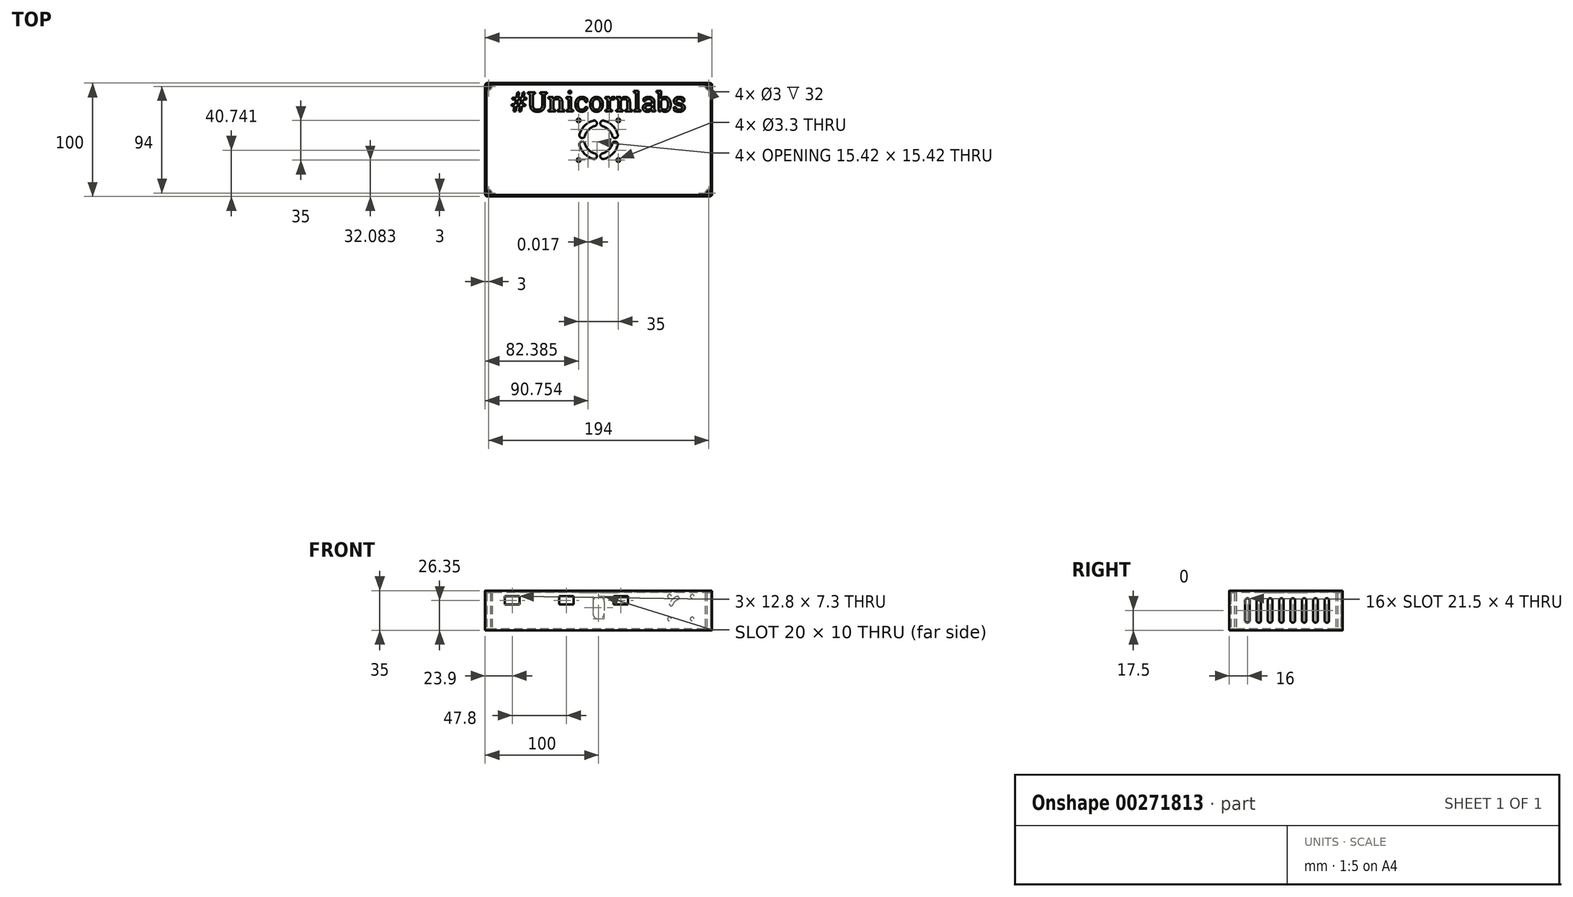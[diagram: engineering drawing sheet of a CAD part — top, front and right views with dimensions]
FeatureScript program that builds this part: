
annotation { "Feature Type Name" : "Feature", "Feature Type Description" : "" }
export const myFeature = defineFeature(function(context is Context, id is Id, definition is map)
    precondition{}
    {
        {
            assignVariable(context, id + "F0", {"name" : "CaseHeight", "anyValue" : 35});
        }
        {
            assignVariable(context, id + "F1", {"name" : "CaseWallThickness", "anyValue" : 1.2});
        }
        {
            assignVariable(context, id + "F2", {"name" : "MetricScrew", "anyValue" : 3});
        }
        {
            var Q0;
            Q0=qCreatedBy(makeId("Top.planeOp"),FACE);
            var sketch = newSketch(context, id + "F3", { "sketchPlane" : qUnion([Q0])});
            skLineSegment(sketch, "E0.bottom", {"start": v(100, 50) * mm, "end": v(-100, 50) * mm});
            skLineSegment(sketch, "E0.top", {"start": v(100, -50) * mm, "end": v(-100, -50) * mm});
            skLineSegment(sketch, "E0.left", {"start": v(100, 50) * mm, "end": v(100, -50) * mm});
            skLineSegment(sketch, "E0.right", {"start": v(-100, 50) * mm, "end": v(-100, -50) * mm});
            skPoint(sketch, "E0.middle", {"position": v(0, 0) * mm});
            skSolve(sketch);
        }
        {
            var Q0;
            Q0=makeQuery(id+"F3.imprint","IMPRINT",FACE,{"disambiguationData":[TD([[makeQuery(id+"F3.imprint","IMPRINT",EDGE,{"derivedFrom":sQuery(id+"F3.wireOp",EDGE,"E0.bottom")}),1.0]])]});
            extrude(context, id + "F4", {"entities" : qUnion([Q0]), "depth" : (getVariable(context, 'CaseHeight')) * mm});
        }
        {
            var Q0;
            Q0=makeQuery(id+"F4.opExtrude","CAP_FACE",FACE,{"disambiguationData":[OSD([sQuery(id+"F3.wireOp",EDGE,"E0.bottom"),sQuery(id+"F3.wireOp",EDGE,"E0.top"),sQuery(id+"F3.wireOp",EDGE,"E0.left"),sQuery(id+"F3.wireOp",EDGE,"E0.right")])],"isStart":false});
            shell(context, id + "F5", {"entities" : qUnion([Q0]), "thickness" : (getVariable(context, 'CaseWallThickness')) * mm});
        }
        {
            var Q0;
            Q0=makeQuery(id+"F5.opShell","OFFSET_FACE",FACE,{"disambiguationData":[OSD([sQuery(id+"F3.wireOp",EDGE,"E0.bottom"),sQuery(id+"F3.wireOp",EDGE,"E0.top"),sQuery(id+"F3.wireOp",EDGE,"E0.left"),sQuery(id+"F3.wireOp",EDGE,"E0.right")])]});
            var sketch = newSketch(context, id + "F6", { "sketchPlane" : qUnion([Q0])});
            skCircle(sketch, "E1", {"center": v(-97, 47) * mm, "radius": 1.5 * mm});
            skCircle(sketch, "E2", {"center": v(97, 47) * mm, "radius": 1.5 * mm});
            skCircle(sketch, "E3", {"center": v(97, -47) * mm, "radius": 1.5 * mm});
            skCircle(sketch, "E4", {"center": v(-97, -47) * mm, "radius": 1.5 * mm});
            skArc(sketch, "E5", {"start": v(-98.8, 44) * mm, "mid": v(-94.88, 44.88) * mm, "end": v(-94, 48.8) * mm});
            skArc(sketch, "E6.MirrorCS", {"start": v(98.8, 44) * mm, "mid": v(94.88, 44.88) * mm, "end": v(94, 48.8) * mm});
            skArc(sketch, "E7.MirrorCS", {"start": v(-98.8, -44) * mm, "mid": v(-94.88, -44.88) * mm, "end": v(-94, -48.8) * mm});
            skArc(sketch, "E8.MirrorCS", {"start": v(98.8, -44) * mm, "mid": v(94.88, -44.88) * mm, "end": v(94, -48.8) * mm});
            skSolve(sketch);
        }
        {
            var Q0;
            Q0=makeQuery(id+"F6.imprint","IMPRINT",FACE,{"disambiguationData":[TD([[makeQuery(id+"F6.imprint","IMPRINT",EDGE,{"derivedFrom":sQuery(id+"F6.wireOp",EDGE,"E1")}),-1.0]])]});
            var Q1;
            Q1=makeQuery(id+"F6.imprint","IMPRINT",FACE,{"disambiguationData":[TD([[makeQuery(id+"F6.imprint","IMPRINT",EDGE,{"derivedFrom":sQuery(id+"F6.wireOp",EDGE,"E2")}),-1.0]])]});
            var Q2;
            Q2=makeQuery(id+"F6.imprint","IMPRINT",FACE,{"disambiguationData":[TD([[makeQuery(id+"F6.imprint","IMPRINT",EDGE,{"derivedFrom":sQuery(id+"F6.wireOp",EDGE,"E3")}),-1.0]])]});
            var Q3;
            Q3=makeQuery(id+"F6.imprint","IMPRINT",FACE,{"disambiguationData":[TD([[makeQuery(id+"F6.imprint","IMPRINT",EDGE,{"derivedFrom":sQuery(id+"F6.wireOp",EDGE,"E4")}),-1.0]])]});
            extrude(context, id + "F7", {"entities" : qUnion([Q0, Q1, Q2, Q3]), "operationType" : NewBodyOperationType.ADD, "depth" : (getVariable(context, 'CaseHeight') - getVariable(context, 'MetricScrew')) * mm});
        }
        {
            var Q0;
            Q0=makeQuery(id+"F7.opExtrude","CAP_FACE",FACE,{"disambiguationData":[OSD([sQuery(id+"F3.wireOp",EDGE,"E0.bottom"),sQuery(id+"F3.wireOp",EDGE,"E0.right"),sQuery(id+"F6.wireOp",EDGE,"E1"),sQuery(id+"F6.wireOp",EDGE,"E5")])],"isStart":false});
            var sketch = newSketch(context, id + "F8", { "sketchPlane" : qUnion([Q0])});
            skPoint(sketch, "E9.0", {"position": v(98.8, -48.8) * mm});
            skPoint(sketch, "E10.0", {"position": v(-98.8, 48.8) * mm});
            skLineSegment(sketch, "E11.bottom", {"start": v(-98.8, 48.8) * mm, "end": v(98.8, 48.8) * mm});
            skLineSegment(sketch, "E11.top", {"start": v(-98.8, -48.8) * mm, "end": v(98.8, -48.8) * mm});
            skLineSegment(sketch, "E11.left", {"start": v(-98.8, 48.8) * mm, "end": v(-98.8, -48.8) * mm});
            skLineSegment(sketch, "E11.right", {"start": v(98.8, 48.8) * mm, "end": v(98.8, -48.8) * mm});
            skCircle(sketch, "E12.0", {"center": v(-97, 47) * mm, "radius": 1.5 * mm});
            skCircle(sketch, "E13.0", {"center": v(97, 47) * mm, "radius": 1.5 * mm});
            skCircle(sketch, "E14.0", {"center": v(97, -47) * mm, "radius": 1.5 * mm});
            skCircle(sketch, "E15.0", {"center": v(-97, -47) * mm, "radius": 1.5 * mm});
            skSolve(sketch);
        }
        {
            var Q0;
            Q0=makeQuery(id+"F8.imprint","IMPRINT",FACE,{"disambiguationData":[TD([[makeQuery(id+"F8.imprint","IMPRINT",EDGE,{"derivedFrom":sQuery(id+"F8.wireOp",EDGE,"E12.0")}),-1.0]])]});
            var Q1;
            {var subQ3=sQuery(id+"F8.wireOp",EDGE,"E11.top");Q1=makeQuery(id+"F8.imprint","IMPRINT",FACE,{"disambiguationData":[TD([[makeQuery(id+"F8.imprint","IMPRINT",EDGE,{"derivedFrom":subQ3}),1.0]])]});}
            extrude(context, id + "F9", {"entities" : qUnion([Q0, Q1]), "depth" : (getVariable(context, 'MetricScrew') / 2) * mm});
        }
        {
            var Q0;
            Q0=makeQuery(id+"F4.opExtrude","SWEPT_FACE",FACE,{"disambiguationData":[OSD([sQuery(id+"F3.wireOp",EDGE,"E0.top")])]});
            var sketch = newSketch(context, id + "F10", { "sketchPlane" : qUnion([Q0])});
            skLineSegment(sketch, "E16.bottom", {"start": v(-69.7, 30) * mm, "end": v(-82.5, 30) * mm});
            skLineSegment(sketch, "E16.top", {"start": v(-69.7, 22.7) * mm, "end": v(-82.5, 22.7) * mm});
            skLineSegment(sketch, "E16.left", {"start": v(-69.7, 30) * mm, "end": v(-69.7, 22.7) * mm});
            skLineSegment(sketch, "E16.right", {"start": v(-82.5, 30) * mm, "end": v(-82.5, 22.7) * mm});
            skPoint(sketch, "E16.middle", {"position": v(-76.1, 26.35) * mm});
            skLineSegment(sketch, "E17.1.0.0", {"start": v(-21.9, 30) * mm, "end": v(-21.9, 22.7) * mm});
            skLineSegment(sketch, "E17.1.0.1", {"start": v(-21.9, 30) * mm, "end": v(-34.7, 30) * mm});
            skLineSegment(sketch, "E17.1.0.2", {"start": v(-34.7, 30) * mm, "end": v(-34.7, 22.7) * mm});
            skLineSegment(sketch, "E17.1.0.3", {"start": v(-21.9, 22.7) * mm, "end": v(-34.7, 22.7) * mm});
            skLineSegment(sketch, "E17.2.0.0", {"start": v(25.9, 30) * mm, "end": v(25.9, 22.7) * mm});
            skLineSegment(sketch, "E17.2.0.1", {"start": v(25.9, 30) * mm, "end": v(13.1, 30) * mm});
            skLineSegment(sketch, "E17.2.0.2", {"start": v(13.1, 30) * mm, "end": v(13.1, 22.7) * mm});
            skLineSegment(sketch, "E17.2.0.3", {"start": v(25.9, 22.7) * mm, "end": v(13.1, 22.7) * mm});
            skLineSegment(sketch, "E17.direction1", {"start": v(-69.7, 22.7) * mm, "end": v(-21.9, 22.7) * mm, "construction": true});
            skSolve(sketch);
        }
        {
            var Q0;
            Q0=qSketchRegion(id+"F10",true);
            extrude(context, id + "F11", {"entities" : qUnion([Q0]), "operationType" : NewBodyOperationType.REMOVE, "oppositeDirection" : true, "depth" : (getVariable(context, 'CaseWallThickness')) * mm});
        }
        {
            var Q0;
            {var subQ0=sQuery(id+"F3.wireOp",EDGE,"E0.right");var subQ1=sQuery(id+"F3.wireOp",EDGE,"E0.left");var subQ2=sQuery(id+"F3.wireOp",EDGE,"E0.top");var subQ3=sQuery(id+"F3.wireOp",EDGE,"E0.bottom");Q0=makeQuery(id+"F7.boolean.opBoolean","SPLIT",FACE,{"disambiguationData":[TD([makeQuery(id+"F5.opShell","OFFSET_FACE",FACE,{"disambiguationData":[OSD([subQ3])]})])],"derivedFrom":makeQuery(id+"F5.opShell","OFFSET_FACE",FACE,{"disambiguationData":[OSD([subQ3,subQ2,subQ1,subQ0])]})});}
            var sketch = newSketch(context, id + "F12", { "sketchPlane" : qUnion([Q0])});
            skLineSegment(sketch, "E18.bottom", {"start": v(-48.8, -43.8) * mm, "end": v(-93.8, -43.8) * mm, "construction": true});
            skLineSegment(sketch, "E18.top", {"start": v(-48.8, -8.8) * mm, "end": v(-93.8, -8.8) * mm, "construction": true});
            skLineSegment(sketch, "E18.left", {"start": v(-48.8, -43.8) * mm, "end": v(-48.8, -8.8) * mm, "construction": true});
            skLineSegment(sketch, "E18.right", {"start": v(-93.8, -43.8) * mm, "end": v(-93.8, -8.8) * mm, "construction": true});
            skPoint(sketch, "E18.middle", {"position": v(-71.3, -26.3) * mm});
            skLineSegment(sketch, "E19.1.0.0", {"start": v(1.2, -8.8) * mm, "end": v(-43.8, -8.8) * mm, "construction": true});
            skLineSegment(sketch, "E19.1.0.1", {"start": v(1.2, -43.8) * mm, "end": v(-43.8, -43.8) * mm, "construction": true});
            skLineSegment(sketch, "E19.1.0.2", {"start": v(1.2, -43.8) * mm, "end": v(1.2, -8.8) * mm, "construction": true});
            skLineSegment(sketch, "E19.1.0.3", {"start": v(-43.8, -43.8) * mm, "end": v(-43.8, -8.8) * mm, "construction": true});
            skPoint(sketch, "E19.1.0.4", {"position": v(-21.3, -26.3) * mm});
            skLineSegment(sketch, "E19.2.0.0", {"start": v(51.2, -8.8) * mm, "end": v(6.2, -8.8) * mm, "construction": true});
            skLineSegment(sketch, "E19.2.0.1", {"start": v(51.2, -43.8) * mm, "end": v(6.2, -43.8) * mm, "construction": true});
            skLineSegment(sketch, "E19.2.0.2", {"start": v(51.2, -43.8) * mm, "end": v(51.2, -8.8) * mm, "construction": true});
            skLineSegment(sketch, "E19.2.0.3", {"start": v(6.2, -43.8) * mm, "end": v(6.2, -8.8) * mm, "construction": true});
            skPoint(sketch, "E19.2.0.4", {"position": v(28.7, -26.3) * mm});
            skLineSegment(sketch, "E19.direction1", {"start": v(-93.8, -43.8) * mm, "end": v(-43.8, -43.8) * mm, "construction": true});
            skLineSegment(sketch, "E20.bottom", {"start": v(81.2, -3.8) * mm, "end": v(1.2, -3.8) * mm, "construction": true});
            skLineSegment(sketch, "E20.top", {"start": v(81.2, 46.2) * mm, "end": v(1.2, 46.2) * mm, "construction": true});
            skLineSegment(sketch, "E20.left", {"start": v(81.2, -3.8) * mm, "end": v(81.2, 46.2) * mm, "construction": true});
            skLineSegment(sketch, "E20.right", {"start": v(1.2, -3.8) * mm, "end": v(1.2, 46.2) * mm, "construction": true});
            skPoint(sketch, "E20.middle", {"position": v(41.2, 21.2) * mm});
            skCircle(sketch, "E21", {"center": v(-53.8, -38.8) * mm, "radius": 2 * mm, "construction": true});
            skCircle(sketch, "E22", {"center": v(-87.8, -38.8) * mm, "radius": 2 * mm, "construction": true});
            skCircle(sketch, "E23.1.0.0", {"center": v(-37.8, -38.8) * mm, "radius": 2 * mm, "construction": true});
            skCircle(sketch, "E23.1.0.1", {"center": v(-3.8, -38.8) * mm, "radius": 2 * mm, "construction": true});
            skLineSegment(sketch, "E23.direction1", {"start": v(-87.8, -38.8) * mm, "end": v(-37.8, -38.8) * mm, "construction": true});
            skCircle(sketch, "E24.0.2.0", {"center": v(12.2, -38.8) * mm, "radius": 2 * mm, "construction": true});
            skCircle(sketch, "E24.2.2.0", {"center": v(46.2, -38.8) * mm, "radius": 2 * mm, "construction": true});
            skLineSegment(sketch, "E25.bottom", {"start": v(-13.8, 52.2) * mm, "end": v(-98.8, 52.2) * mm, "construction": true});
            skLineSegment(sketch, "E25.top", {"start": v(-13.8, -3.8) * mm, "end": v(-98.8, -3.8) * mm, "construction": true});
            skLineSegment(sketch, "E25.left", {"start": v(-13.8, 52.2) * mm, "end": v(-13.8, -3.8) * mm, "construction": true});
            skLineSegment(sketch, "E25.right", {"start": v(-98.8, 52.2) * mm, "end": v(-98.8, -3.8) * mm, "construction": true});
            skCircle(sketch, "E26", {"center": v(-17.3, 48.7) * mm, "radius": 1.25 * mm, "construction": true});
            skCircle(sketch, "E27", {"center": v(-17.3, -0.3) * mm, "radius": 1.25 * mm, "construction": true});
            skCircle(sketch, "E28", {"center": v(-75.3, 48.7) * mm, "radius": 1.25 * mm, "construction": true});
            skCircle(sketch, "E29", {"center": v(-75.3, -0.3) * mm, "radius": 1.25 * mm, "construction": true});
            skLineSegment(sketch, "E30.bottom", {"start": v(-98.8, 47.03) * mm, "end": v(-84.72, 47.03) * mm, "construction": true});
            skLineSegment(sketch, "E30.top", {"start": v(-98.8, 33) * mm, "end": v(-84.72, 33) * mm, "construction": true});
            skLineSegment(sketch, "E30.left", {"start": v(-98.8, 47.03) * mm, "end": v(-98.8, 33) * mm, "construction": true});
            skLineSegment(sketch, "E30.right", {"start": v(-84.72, 47.03) * mm, "end": v(-84.72, 33) * mm, "construction": true});
            skLineSegment(sketch, "E31.bottom", {"start": v(-98.8, 26.34) * mm, "end": v(-82.63, 26.34) * mm, "construction": true});
            skLineSegment(sketch, "E31.top", {"start": v(-98.8, 15.16) * mm, "end": v(-82.63, 15.16) * mm, "construction": true});
            skLineSegment(sketch, "E31.left", {"start": v(-98.8, 26.34) * mm, "end": v(-98.8, 15.16) * mm, "construction": true});
            skLineSegment(sketch, "E31.right", {"start": v(-82.63, 26.34) * mm, "end": v(-82.63, 15.16) * mm, "construction": true});
            skLineSegment(sketch, "E32.bottom", {"start": v(-98.8, 11.68) * mm, "end": v(-82.2, 11.68) * mm, "construction": true});
            skLineSegment(sketch, "E32.top", {"start": v(-98.8, 2.22) * mm, "end": v(-82.2, 2.22) * mm, "construction": true});
            skLineSegment(sketch, "E32.left", {"start": v(-98.8, 11.68) * mm, "end": v(-98.8, 2.22) * mm, "construction": true});
            skLineSegment(sketch, "E32.right", {"start": v(-82.2, 11.68) * mm, "end": v(-82.2, 2.22) * mm, "construction": true});
            skLineSegment(sketch, "E33.bottom", {"start": v(-95.5, -3.8) * mm, "end": v(-102, -3.8) * mm, "construction": true});
            skLineSegment(sketch, "E33.top", {"start": v(-95.5, -1.49) * mm, "end": v(-102, -1.49) * mm, "construction": true});
            skLineSegment(sketch, "E33.left", {"start": v(-95.5, -3.8) * mm, "end": v(-95.5, -1.49) * mm, "construction": true});
            skLineSegment(sketch, "E33.right", {"start": v(-102, -3.8) * mm, "end": v(-102, -1.49) * mm, "construction": true});
            skSolve(sketch);
        }
        {
            var Q0;
            Q0=makeQuery(id+"F5.opShell","OFFSET_FACE",FACE,{"disambiguationData":[OSD([sQuery(id+"F3.wireOp",EDGE,"E0.bottom")])]});
            var sketch = newSketch(context, id + "F13", { "sketchPlane" : qUnion([Q0])});
            skLineSegment(sketch, "E34.bottom", {"start": v(60, 32.5) * mm, "end": v(85, 32.5) * mm, "construction": true});
            skLineSegment(sketch, "E34.top", {"start": v(60, 7.5) * mm, "end": v(85, 7.5) * mm, "construction": true});
            skLineSegment(sketch, "E34.left", {"start": v(60, 32.5) * mm, "end": v(60, 7.5) * mm, "construction": true});
            skLineSegment(sketch, "E34.right", {"start": v(85, 32.5) * mm, "end": v(85, 7.5) * mm, "construction": true});
            skPoint(sketch, "E34.middle", {"position": v(72.5, 20) * mm});
            skCircle(sketch, "E35", {"center": v(72.5, 20) * mm, "radius": 12.5 * mm});
            skCircle(sketch, "E36", {"center": v(72.5, 20) * mm, "radius": 5 * mm, "construction": true});
            skArc(sketch, "E37", {"start": v(69.5, 28.49) * mm, "mid": v(66.14, 26.36) * mm, "end": v(64.01, 23) * mm, "construction": true});
            skArc(sketch, "E38.1.0", {"start": v(64.01, 17) * mm, "mid": v(66.14, 13.64) * mm, "end": v(69.5, 11.51) * mm, "construction": true});
            skArc(sketch, "E38.2.0", {"start": v(75.5, 11.51) * mm, "mid": v(78.86, 13.64) * mm, "end": v(80.99, 17) * mm, "construction": true});
            skArc(sketch, "E38.3.0", {"start": v(80.99, 23) * mm, "mid": v(78.86, 26.36) * mm, "end": v(75.5, 28.49) * mm, "construction": true});
            skArc(sketch, "E39.0", {"start": v(70, 27.07) * mm, "mid": v(67.2, 25.3) * mm, "end": v(65.43, 22.5) * mm});
            skArc(sketch, "E40.0", {"start": v(69, 29.9) * mm, "mid": v(65.08, 27.42) * mm, "end": v(62.6, 23.5) * mm});
            skArc(sketch, "E41", {"start": v(62.6, 23.5) * mm, "mid": v(63.51, 21.59) * mm, "end": v(65.43, 22.5) * mm});
            skArc(sketch, "E42", {"start": v(70, 27.07) * mm, "mid": v(70.91, 28.99) * mm, "end": v(69, 29.9) * mm});
            skPoint(sketch, "E43", {"position": v(62.5, 30) * mm});
            skPoint(sketch, "E44", {"position": v(82.5, 30) * mm});
            skPoint(sketch, "E45", {"position": v(82.5, 10) * mm});
            skPoint(sketch, "E46", {"position": v(62.5, 10) * mm});
            skLineSegment(sketch, "E47", {"start": v(72.5, 20) * mm, "end": v(72.5, 28.33) * mm, "construction": true});
            skLineSegment(sketch, "E48", {"start": v(72.5, 20) * mm, "end": v(63.9, 20) * mm, "construction": true});
            skSolve(sketch);
        }
        {
            var Q0;
            Q0=makeQuery(id+"F13.imprint","IMPRINT",FACE,{"disambiguationData":[TD([[makeQuery(id+"F13.imprint","IMPRINT",EDGE,{"derivedFrom":sQuery(id+"F13.wireOp",EDGE,"E35")}),-1.0]])]});
            var sketch = newSketch(context, id + "F14", { "sketchPlane" : qUnion([Q0])});
            skLineSegment(sketch, "E49", {"start": v(0, 25) * mm, "end": v(0, 15) * mm});
            skArc(sketch, "E50.0.startCap", {"start": v(-5, 25) * mm, "mid": v(0, 30) * mm, "end": v(5, 25) * mm});
            skArc(sketch, "E50.0.endCap", {"start": v(5, 15) * mm, "mid": v(0, 10) * mm, "end": v(-5, 15) * mm});
            skLineSegment(sketch, "E50.0.left", {"start": v(5, 25) * mm, "end": v(5, 15) * mm});
            skLineSegment(sketch, "E50.0.right", {"start": v(-5, 25) * mm, "end": v(-5, 15) * mm});
            skSolve(sketch);
        }
        {
            var Q0;
            Q0=qSketchRegion(id+"F14",true);
            extrude(context, id + "F15", {"entities" : qUnion([Q0]), "operationType" : NewBodyOperationType.REMOVE, "oppositeDirection" : true, "depth" : (getVariable(context, 'CaseWallThickness')) * mm});
        }
        {
            var Q0;
            Q0=makeQuery(id+"F4.opExtrude","SWEPT_FACE",FACE,{"disambiguationData":[OSD([sQuery(id+"F3.wireOp",EDGE,"E0.right")])]});
            var sketch = newSketch(context, id + "F16", { "sketchPlane" : qUnion([Q0])});
            skLineSegment(sketch, "E51", {"start": v(-36, 26.25) * mm, "end": v(-36, 8.75) * mm});
            skArc(sketch, "E52.0.startCap", {"start": v(-38, 26.25) * mm, "mid": v(-36, 28.25) * mm, "end": v(-34, 26.25) * mm});
            skArc(sketch, "E52.0.endCap", {"start": v(-34, 8.75) * mm, "mid": v(-36, 6.75) * mm, "end": v(-38, 8.75) * mm});
            skLineSegment(sketch, "E52.0.left", {"start": v(-34, 26.25) * mm, "end": v(-34, 8.75) * mm});
            skLineSegment(sketch, "E52.0.right", {"start": v(-38, 26.25) * mm, "end": v(-38, 8.75) * mm});
            skLineSegment(sketch, "E53.1.0.0", {"start": v(-28, 26.25) * mm, "end": v(-28, 8.75) * mm});
            skLineSegment(sketch, "E53.1.0.1", {"start": v(-24, 26.25) * mm, "end": v(-24, 8.75) * mm});
            skArc(sketch, "E53.1.0.2", {"start": v(-24, 8.75) * mm, "mid": v(-26, 6.75) * mm, "end": v(-28, 8.75) * mm});
            skArc(sketch, "E53.1.0.3", {"start": v(-28, 26.25) * mm, "mid": v(-26, 28.25) * mm, "end": v(-24, 26.25) * mm});
            skLineSegment(sketch, "E53.1.0.4", {"start": v(-26, 26.25) * mm, "end": v(-26, 8.75) * mm});
            skLineSegment(sketch, "E53.2.0.0", {"start": v(-18, 26.25) * mm, "end": v(-18, 8.75) * mm});
            skLineSegment(sketch, "E53.2.0.1", {"start": v(-14, 26.25) * mm, "end": v(-14, 8.75) * mm});
            skArc(sketch, "E53.2.0.2", {"start": v(-14, 8.75) * mm, "mid": v(-16, 6.75) * mm, "end": v(-18, 8.75) * mm});
            skArc(sketch, "E53.2.0.3", {"start": v(-18, 26.25) * mm, "mid": v(-16, 28.25) * mm, "end": v(-14, 26.25) * mm});
            skLineSegment(sketch, "E53.2.0.4", {"start": v(-16, 26.25) * mm, "end": v(-16, 8.75) * mm});
            skLineSegment(sketch, "E53.3.0.0", {"start": v(-8, 26.25) * mm, "end": v(-8, 8.75) * mm});
            skLineSegment(sketch, "E53.3.0.1", {"start": v(-4, 26.25) * mm, "end": v(-4, 8.75) * mm});
            skArc(sketch, "E53.3.0.2", {"start": v(-4, 8.75) * mm, "mid": v(-6, 6.75) * mm, "end": v(-8, 8.75) * mm});
            skArc(sketch, "E53.3.0.3", {"start": v(-8, 26.25) * mm, "mid": v(-6, 28.25) * mm, "end": v(-4, 26.25) * mm});
            skLineSegment(sketch, "E53.3.0.4", {"start": v(-6, 26.25) * mm, "end": v(-6, 8.75) * mm});
            skLineSegment(sketch, "E53.4.0.0", {"start": v(2, 26.25) * mm, "end": v(2, 8.75) * mm});
            skLineSegment(sketch, "E53.4.0.1", {"start": v(6, 26.25) * mm, "end": v(6, 8.75) * mm});
            skArc(sketch, "E53.4.0.2", {"start": v(6, 8.75) * mm, "mid": v(4, 6.75) * mm, "end": v(2, 8.75) * mm});
            skArc(sketch, "E53.4.0.3", {"start": v(2, 26.25) * mm, "mid": v(4, 28.25) * mm, "end": v(6, 26.25) * mm});
            skLineSegment(sketch, "E53.4.0.4", {"start": v(4, 26.25) * mm, "end": v(4, 8.75) * mm});
            skLineSegment(sketch, "E53.5.0.0", {"start": v(12, 26.25) * mm, "end": v(12, 8.75) * mm});
            skLineSegment(sketch, "E53.5.0.1", {"start": v(16, 26.25) * mm, "end": v(16, 8.75) * mm});
            skArc(sketch, "E53.5.0.2", {"start": v(16, 8.75) * mm, "mid": v(14, 6.75) * mm, "end": v(12, 8.75) * mm});
            skArc(sketch, "E53.5.0.3", {"start": v(12, 26.25) * mm, "mid": v(14, 28.25) * mm, "end": v(16, 26.25) * mm});
            skLineSegment(sketch, "E53.5.0.4", {"start": v(14, 26.25) * mm, "end": v(14, 8.75) * mm});
            skLineSegment(sketch, "E53.6.0.0", {"start": v(22, 26.25) * mm, "end": v(22, 8.75) * mm});
            skLineSegment(sketch, "E53.6.0.1", {"start": v(26, 26.25) * mm, "end": v(26, 8.75) * mm});
            skArc(sketch, "E53.6.0.2", {"start": v(26, 8.75) * mm, "mid": v(24, 6.75) * mm, "end": v(22, 8.75) * mm});
            skArc(sketch, "E53.6.0.3", {"start": v(22, 26.25) * mm, "mid": v(24, 28.25) * mm, "end": v(26, 26.25) * mm});
            skLineSegment(sketch, "E53.6.0.4", {"start": v(24, 26.25) * mm, "end": v(24, 8.75) * mm});
            skLineSegment(sketch, "E53.7.0.0", {"start": v(32, 26.25) * mm, "end": v(32, 8.75) * mm});
            skLineSegment(sketch, "E53.7.0.1", {"start": v(36, 26.25) * mm, "end": v(36, 8.75) * mm});
            skArc(sketch, "E53.7.0.2", {"start": v(36, 8.75) * mm, "mid": v(34, 6.75) * mm, "end": v(32, 8.75) * mm});
            skArc(sketch, "E53.7.0.3", {"start": v(32, 26.25) * mm, "mid": v(34, 28.25) * mm, "end": v(36, 26.25) * mm});
            skLineSegment(sketch, "E53.7.0.4", {"start": v(34, 26.25) * mm, "end": v(34, 8.75) * mm});
            skLineSegment(sketch, "E53.direction1", {"start": v(-38, 8.75) * mm, "end": v(-28, 8.75) * mm, "construction": true});
            skSolve(sketch);
        }
        {
            var Q0;
            Q0=qSketchRegion(id+"F16",true);
            extrude(context, id + "F17", {"entities" : qUnion([Q0]), "operationType" : NewBodyOperationType.REMOVE, "endBound" : BoundingType.THROUGH_ALL, "oppositeDirection" : true, "depth" : 25 * mm});
        }
        {
            var Q0;
            Q0=makeQuery(id+"F4.opExtrude","SWEPT_EDGE",EDGE,{"disambiguationData":[OSD([sQuery(id+"F3.wireOp",EDGE,"E0.bottom"),sQuery(id+"F3.wireOp",EDGE,"E0.right")])]});
            var Q1;
            Q1=makeQuery(id+"F4.opExtrude","SWEPT_EDGE",EDGE,{"disambiguationData":[OSD([sQuery(id+"F3.wireOp",EDGE,"E0.top"),sQuery(id+"F3.wireOp",EDGE,"E0.right")])]});
            var Q2;
            Q2=makeQuery(id+"F4.opExtrude","SWEPT_EDGE",EDGE,{"disambiguationData":[OSD([sQuery(id+"F3.wireOp",EDGE,"E0.top"),sQuery(id+"F3.wireOp",EDGE,"E0.left")])]});
            var Q3;
            Q3=makeQuery(id+"F4.opExtrude","SWEPT_EDGE",EDGE,{"disambiguationData":[OSD([sQuery(id+"F3.wireOp",EDGE,"E0.bottom"),sQuery(id+"F3.wireOp",EDGE,"E0.left")])]});
            fillet(context, id + "F18", {"entities" : qUnion([Q0, Q1, Q2, Q3]), "radius" : 2 * mm, "tangentPropagation" : true, "allowEdgeOverflow" : false});
        }
        {
            var Q0;
            Q0=makeQuery(id+"F9.opExtrude","CAP_FACE",FACE,{"disambiguationData":[OSD([sQuery(id+"F8.wireOp",EDGE,"E11.bottom"),sQuery(id+"F8.wireOp",EDGE,"E11.top"),sQuery(id+"F8.wireOp",EDGE,"E11.left"),sQuery(id+"F8.wireOp",EDGE,"E11.right"),sQuery(id+"F8.wireOp",EDGE,"E12.0"),sQuery(id+"F8.wireOp",EDGE,"E13.0"),sQuery(id+"F8.wireOp",EDGE,"E14.0"),sQuery(id+"F8.wireOp",EDGE,"E15.0")])],"isStart":false});
            var sketch = newSketch(context, id + "F19", { "sketchPlane" : qUnion([Q0])});
            skCircle(sketch, "E54", {"center": v(0, 0) * mm, "radius": 20 * mm});
            skLineSegment(sketch, "E55.bottom", {"start": v(20, 20) * mm, "end": v(-20, 20) * mm, "construction": true});
            skLineSegment(sketch, "E55.top", {"start": v(20, -20) * mm, "end": v(-20, -20) * mm, "construction": true});
            skLineSegment(sketch, "E55.left", {"start": v(20, 20) * mm, "end": v(20, -20) * mm, "construction": true});
            skLineSegment(sketch, "E55.right", {"start": v(-20, 20) * mm, "end": v(-20, -20) * mm, "construction": true});
            skLineSegment(sketch, "E56", {"start": v(-20, 0) * mm, "end": v(20, 0) * mm, "construction": true});
            skLineSegment(sketch, "E57", {"start": v(0, 20) * mm, "end": v(0, -20) * mm, "construction": true});
            skLineSegment(sketch, "E58.0.0", {"start": v(98.8, 48.8) * mm, "end": v(-98.8, 48.8) * mm});
            skLineSegment(sketch, "E58.0.1", {"start": v(-98.8, 48.8) * mm, "end": v(-98.8, -48.8) * mm});
            skLineSegment(sketch, "E58.0.2", {"start": v(-98.8, -48.8) * mm, "end": v(98.8, -48.8) * mm});
            skLineSegment(sketch, "E58.0.3", {"start": v(98.8, -48.8) * mm, "end": v(98.8, 48.8) * mm});
            skArc(sketch, "E59", {"start": v(-4, 14.46) * mm, "mid": v(-10.6, 10.6) * mm, "end": v(-14.46, 4) * mm, "construction": true});
            skArc(sketch, "E60.0", {"start": v(-3.33, 12.05) * mm, "mid": v(-8.84, 8.84) * mm, "end": v(-12.05, 3.33) * mm});
            skArc(sketch, "E61.0", {"start": v(-4.67, 16.87) * mm, "mid": v(-12.37, 12.37) * mm, "end": v(-16.87, 4.67) * mm});
            skArc(sketch, "E62", {"start": v(-3.33, 12.05) * mm, "mid": v(-1.6, 15.12) * mm, "end": v(-4.67, 16.87) * mm});
            skArc(sketch, "E63", {"start": v(-16.87, 4.67) * mm, "mid": v(-15.12, 1.6) * mm, "end": v(-12.05, 3.33) * mm});
            skLineSegment(sketch, "E64", {"start": v(-16.87, 4.67) * mm, "end": v(-12.05, 3.33) * mm, "construction": true});
            skLineSegment(sketch, "E65", {"start": v(-4.67, 16.87) * mm, "end": v(-3.33, 12.05) * mm, "construction": true});
            skPoint(sketch, "E66", {"position": v(-17.62, 17.08) * mm});
            skPoint(sketch, "E67", {"position": v(17.38, 17.08) * mm});
            skPoint(sketch, "E68", {"position": v(17.38, -17.92) * mm});
            skPoint(sketch, "E69", {"position": v(-17.62, -17.92) * mm});
            skArc(sketch, "E70.1.0", {"start": v(-12.06, -3.36) * mm, "mid": v(-15.14, -1.62) * mm, "end": v(-16.88, -4.7) * mm});
            skArc(sketch, "E70.1.1", {"start": v(-14.47, -4.03) * mm, "mid": v(-10.62, -10.64) * mm, "end": v(-4.02, -14.49) * mm, "construction": true});
            skLineSegment(sketch, "E70.1.2", {"start": v(-16.88, -4.7) * mm, "end": v(-12.06, -3.36) * mm, "construction": true});
            skArc(sketch, "E70.1.3", {"start": v(-16.88, -4.7) * mm, "mid": v(-12.4, -12.4) * mm, "end": v(-4.68, -16.9) * mm});
            skArc(sketch, "E70.1.4", {"start": v(-12.06, -3.36) * mm, "mid": v(-8.86, -8.87) * mm, "end": v(-3.35, -12.08) * mm});
            skArc(sketch, "E70.1.5", {"start": v(-4.68, -16.9) * mm, "mid": v(-1.6, -15.15) * mm, "end": v(-3.35, -12.08) * mm});
            skLineSegment(sketch, "E70.1.6", {"start": v(-4.68, -16.9) * mm, "end": v(-3.35, -12.08) * mm, "construction": true});
            skArc(sketch, "E70.2.0", {"start": v(3.35, -12.1) * mm, "mid": v(1.6, -15.17) * mm, "end": v(4.68, -16.91) * mm});
            skArc(sketch, "E70.2.1", {"start": v(4.01, -14.5) * mm, "mid": v(10.62, -10.65) * mm, "end": v(14.47, -4.05) * mm, "construction": true});
            skLineSegment(sketch, "E70.2.2", {"start": v(4.68, -16.91) * mm, "end": v(3.35, -12.1) * mm, "construction": true});
            skArc(sketch, "E70.2.3", {"start": v(4.68, -16.91) * mm, "mid": v(12.39, -12.42) * mm, "end": v(16.88, -4.71) * mm});
            skArc(sketch, "E70.2.4", {"start": v(3.35, -12.1) * mm, "mid": v(8.85, -8.89) * mm, "end": v(12.06, -3.38) * mm});
            skArc(sketch, "E70.2.5", {"start": v(16.88, -4.71) * mm, "mid": v(15.14, -1.64) * mm, "end": v(12.06, -3.38) * mm});
            skLineSegment(sketch, "E70.2.6", {"start": v(16.88, -4.71) * mm, "end": v(12.06, -3.38) * mm, "construction": true});
            skArc(sketch, "E70.3.0", {"start": v(12.08, 3.32) * mm, "mid": v(15.15, 1.57) * mm, "end": v(16.9, 4.65) * mm});
            skArc(sketch, "E70.3.1", {"start": v(14.49, 3.98) * mm, "mid": v(10.64, 10.59) * mm, "end": v(4.03, 14.44) * mm, "construction": true});
            skLineSegment(sketch, "E70.3.2", {"start": v(16.9, 4.65) * mm, "end": v(12.08, 3.32) * mm, "construction": true});
            skArc(sketch, "E70.3.3", {"start": v(16.9, 4.65) * mm, "mid": v(12.4, 12.36) * mm, "end": v(4.7, 16.85) * mm});
            skArc(sketch, "E70.3.4", {"start": v(12.08, 3.32) * mm, "mid": v(8.87, 8.82) * mm, "end": v(3.36, 12.03) * mm});
            skArc(sketch, "E70.3.5", {"start": v(4.7, 16.85) * mm, "mid": v(1.62, 15.1) * mm, "end": v(3.36, 12.03) * mm});
            skLineSegment(sketch, "E70.3.6", {"start": v(4.7, 16.85) * mm, "end": v(3.36, 12.03) * mm, "construction": true});
            skPoint(sketch, "E70.center", {"position": v(0, -0.02) * mm});
            skSolve(sketch);
        }
        {
            var Q0;
            Q0=makeQuery(id+"F13.imprint","IMPRINT",FACE,{"disambiguationData":[TD([[makeQuery(id+"F13.imprint","IMPRINT",EDGE,{"derivedFrom":sQuery(id+"F13.wireOp",EDGE,"E39.0")}),-1.0]])]});
            extrude(context, id + "F20", {"entities" : qUnion([Q0]), "operationType" : NewBodyOperationType.REMOVE, "oppositeDirection" : true, "depth" : (getVariable(context, 'CaseWallThickness')) * mm});
        }
        {
            var Q0;
            Q0=makeQuery(id+"F4.opExtrude","CAP_FACE",FACE,{"disambiguationData":[OSD([sQuery(id+"F3.wireOp",EDGE,"E0.bottom"),sQuery(id+"F3.wireOp",EDGE,"E0.top"),sQuery(id+"F3.wireOp",EDGE,"E0.left"),sQuery(id+"F3.wireOp",EDGE,"E0.right")])],"isStart":false});
            cPlane(context, id + "F21", {"entities" : qUnion([Q0]), "cplaneType" : CPlaneType.OFFSET, "offset" : 15 * mm, "oppositeDirection" : true, "width" : 150 * mm, "height" : 150 * mm});
        }
        {
            var Q0;
            Q0=qCreatedBy(id+"F21.planeOp",FACE);
            var sketch = newSketch(context, id + "F22", { "sketchPlane" : qUnion([Q0])});
            skPoint(sketch, "E71.0", {"position": v(72.5, 48.8) * mm});
            skLineSegment(sketch, "E72", {"start": v(72.5, 48.8) * mm, "end": v(72.5, 70) * mm, "construction": true});
            skSolve(sketch);
        }
        {
            var Q0;
            Q0=sQuery(id+"F13.wireOp",VERTEX,"E43");
            var Q1;
            Q1=sQuery(id+"F13.wireOp",VERTEX,"E44");
            var Q2;
            Q2=sQuery(id+"F13.wireOp",VERTEX,"E45");
            var Q3;
            Q3=sQuery(id+"F13.wireOp",VERTEX,"E46");
            var Q4;
            Q4=makeQuery(id+"F4.opExtrude","SWEPT_BODY",BODY,{"disambiguationData":[OSD([sQuery(id+"F3.wireOp",EDGE,"E0.bottom"),sQuery(id+"F3.wireOp",EDGE,"E0.top"),sQuery(id+"F3.wireOp",EDGE,"E0.left"),sQuery(id+"F3.wireOp",EDGE,"E0.right")])]});
            hole(context, id + "F23", {"style" : HoleStyle.SIMPLE, "endStyle" : HoleEndStyle.BLIND, "standardTappedOrClearance" : lookupTablePath({ "standard" : "ISO", "fit" : "Normal", "size" : "M3", "type" : "Clearance" }), "standardBlindInLast" : lookupTablePath({ "fit" : "Standard", "standard" : "ISO", "size" : "M3", "type" : "Clearance" }), "holeDiameter" : 3.3 * mm, "holeDepth" : (getVariable(context, 'CaseWallThickness')) * mm, "startFromSketch" : true, "locations" : qUnion([Q0, Q1, Q2, Q3]), "scope" : qUnion([Q4])});
        }
        {
            var Q0;
            Q0=makeQuery(id+"F19.imprint","IMPRINT",FACE,{"disambiguationData":[TD([[makeQuery(id+"F19.imprint","IMPRINT",EDGE,{"derivedFrom":sQuery(id+"F19.wireOp",EDGE,"E60.0")}),-1.0]])]});
            var Q1;
            Q1=makeQuery(id+"F19.imprint","IMPRINT",FACE,{"disambiguationData":[TD([[makeQuery(id+"F19.imprint","IMPRINT",EDGE,{"derivedFrom":sQuery(id+"F19.wireOp",EDGE,"E70.3.0")}),1.0]])]});
            var Q2;
            Q2=makeQuery(id+"F19.imprint","IMPRINT",FACE,{"disambiguationData":[TD([[makeQuery(id+"F19.imprint","IMPRINT",EDGE,{"derivedFrom":sQuery(id+"F19.wireOp",EDGE,"E70.2.0")}),1.0]])]});
            var Q3;
            Q3=makeQuery(id+"F19.imprint","IMPRINT",FACE,{"disambiguationData":[TD([[makeQuery(id+"F19.imprint","IMPRINT",EDGE,{"derivedFrom":sQuery(id+"F19.wireOp",EDGE,"E70.1.0")}),1.0]])]});
            extrude(context, id + "F24", {"entities" : qUnion([Q0, Q1, Q2, Q3]), "operationType" : NewBodyOperationType.REMOVE, "oppositeDirection" : true, "depth" : (getVariable(context, 'MetricScrew') / 2) * mm});
        }
        {
            var Q0;
            Q0=sQuery(id+"F19.wireOp",VERTEX,"E66");
            var Q1;
            Q1=sQuery(id+"F19.wireOp",VERTEX,"E67");
            var Q2;
            Q2=sQuery(id+"F19.wireOp",VERTEX,"E68");
            var Q3;
            Q3=sQuery(id+"F19.wireOp",VERTEX,"E69");
            var Q4;
            Q4=makeQuery(id+"F9.opExtrude","SWEPT_BODY",BODY,{"disambiguationData":[OSD([sQuery(id+"F8.wireOp",EDGE,"E11.bottom"),sQuery(id+"F8.wireOp",EDGE,"E11.top"),sQuery(id+"F8.wireOp",EDGE,"E11.left"),sQuery(id+"F8.wireOp",EDGE,"E11.right"),sQuery(id+"F8.wireOp",EDGE,"E12.0"),sQuery(id+"F8.wireOp",EDGE,"E13.0"),sQuery(id+"F8.wireOp",EDGE,"E14.0"),sQuery(id+"F8.wireOp",EDGE,"E15.0")])]});
            hole(context, id + "F25", {"style" : HoleStyle.SIMPLE, "endStyle" : HoleEndStyle.BLIND, "standardTappedOrClearance" : lookupTablePath({ "standard" : "ISO", "fit" : "Normal", "size" : "M3", "type" : "Clearance" }), "standardBlindInLast" : lookupTablePath({ "fit" : "Standard", "standard" : "ISO", "size" : "M3", "type" : "Clearance" }), "holeDiameter" : 3.3 * mm, "holeDepth" : (getVariable(context, 'MetricScrew') / 2) * mm, "startFromSketch" : true, "locations" : qUnion([Q0, Q1, Q2, Q3]), "scope" : qUnion([Q4])});
        }
        {
            var Q0;
            Q0=makeQuery(id+"F9.opExtrude","CAP_FACE",FACE,{"disambiguationData":[OSD([sQuery(id+"F8.wireOp",EDGE,"E11.bottom"),sQuery(id+"F8.wireOp",EDGE,"E11.top"),sQuery(id+"F8.wireOp",EDGE,"E11.left"),sQuery(id+"F8.wireOp",EDGE,"E11.right"),sQuery(id+"F8.wireOp",EDGE,"E12.0"),sQuery(id+"F8.wireOp",EDGE,"E13.0"),sQuery(id+"F8.wireOp",EDGE,"E14.0"),sQuery(id+"F8.wireOp",EDGE,"E15.0")])],"isStart":false});
            var sketch = newSketch(context, id + "F26", { "sketchPlane" : qUnion([Q0])});
            skText(sketch, "E73", { "text": "#Unicornlabs", "fontName": "RobotoSlab-Regular.ttf"});
            skLineSegment(sketch, "E74.0.0", {"start": v(98.8, 48.8) * mm, "end": v(-98.8, 48.8) * mm});
            skLineSegment(sketch, "E74.0.1", {"start": v(-98.8, 48.8) * mm, "end": v(-98.8, -48.8) * mm});
            skLineSegment(sketch, "E74.0.2", {"start": v(-98.8, -48.8) * mm, "end": v(98.8, -48.8) * mm});
            skLineSegment(sketch, "E74.0.3", {"start": v(98.8, -48.8) * mm, "end": v(98.8, 48.8) * mm});
            const initialGuessF26  = {"E73": [-0.0775, 0.02488, 1, 0, 0.01727]};
            skSetInitialGuess(sketch, initialGuessF26);
            skSolve(sketch);
        }
        {
            var Q0;
            Q0=makeQuery(id+"F26.imprint","IMPRINT",FACE,{"disambiguationData":[TD([[makeQuery(id+"F26.imprint","IMPRINT",EDGE,{"derivedFrom":sQuery(id+"F26.wireOp",EDGE,"E73.sketch_text.stroke-32")}),-1.0]])]});
            var Q1;
            Q1=makeQuery(id+"F26.imprint","IMPRINT",FACE,{"disambiguationData":[TD([[makeQuery(id+"F26.imprint","IMPRINT",EDGE,{"derivedFrom":sQuery(id+"F26.wireOp",EDGE,"E73.sketch_text.stroke-0")}),-1.0]])]});
            var Q2;
            Q2=makeQuery(id+"F26.imprint","IMPRINT",FACE,{"disambiguationData":[TD([[makeQuery(id+"F26.imprint","IMPRINT",EDGE,{"derivedFrom":sQuery(id+"F26.wireOp",EDGE,"E73.sketch_text.stroke-56")}),-1.0]])]});
            var Q3;
            Q3=makeQuery(id+"F26.imprint","IMPRINT",FACE,{"disambiguationData":[TD([[makeQuery(id+"F26.imprint","IMPRINT",EDGE,{"derivedFrom":sQuery(id+"F26.wireOp",EDGE,"E73.sketch_text.stroke-82")}),-1.0]])]});
            var Q4;
            Q4=makeQuery(id+"F26.imprint","IMPRINT",FACE,{"disambiguationData":[TD([[makeQuery(id+"F26.imprint","IMPRINT",EDGE,{"derivedFrom":sQuery(id+"F26.wireOp",EDGE,"E73.sketch_text.stroke-92")}),-1.0]])]});
            var Q5;
            Q5=makeQuery(id+"F26.imprint","IMPRINT",FACE,{"disambiguationData":[TD([[makeQuery(id+"F26.imprint","IMPRINT",EDGE,{"derivedFrom":sQuery(id+"F26.wireOp",EDGE,"E73.sketch_text.stroke-96")}),-1.0]])]});
            var Q6;
            Q6=makeQuery(id+"F26.imprint","IMPRINT",FACE,{"disambiguationData":[TD([[makeQuery(id+"F26.imprint","IMPRINT",EDGE,{"derivedFrom":sQuery(id+"F26.wireOp",EDGE,"E73.sketch_text.stroke-119")}),-1.0]])]});
            var Q7;
            Q7=makeQuery(id+"F26.imprint","IMPRINT",FACE,{"disambiguationData":[TD([[makeQuery(id+"F26.imprint","IMPRINT",EDGE,{"derivedFrom":sQuery(id+"F26.wireOp",EDGE,"E73.sketch_text.stroke-139")}),-1.0]])]});
            var Q8;
            Q8=makeQuery(id+"F26.imprint","IMPRINT",FACE,{"disambiguationData":[TD([[makeQuery(id+"F26.imprint","IMPRINT",EDGE,{"derivedFrom":sQuery(id+"F26.wireOp",EDGE,"E73.sketch_text.stroke-158")}),-1.0]])]});
            var Q9;
            Q9=makeQuery(id+"F26.imprint","IMPRINT",FACE,{"disambiguationData":[TD([[makeQuery(id+"F26.imprint","IMPRINT",EDGE,{"derivedFrom":sQuery(id+"F26.wireOp",EDGE,"E73.sketch_text.stroke-184")}),-1.0]])]});
            var Q10;
            Q10=makeQuery(id+"F26.imprint","IMPRINT",FACE,{"disambiguationData":[TD([[makeQuery(id+"F26.imprint","IMPRINT",EDGE,{"derivedFrom":sQuery(id+"F26.wireOp",EDGE,"E73.sketch_text.stroke-194")}),-1.0]])]});
            var Q11;
            Q11=makeQuery(id+"F26.imprint","IMPRINT",FACE,{"disambiguationData":[TD([[makeQuery(id+"F26.imprint","IMPRINT",EDGE,{"derivedFrom":sQuery(id+"F26.wireOp",EDGE,"E73.sketch_text.stroke-229")}),-1.0]])]});
            var Q12;
            Q12=makeQuery(id+"F26.imprint","IMPRINT",FACE,{"disambiguationData":[TD([[makeQuery(id+"F26.imprint","IMPRINT",EDGE,{"derivedFrom":sQuery(id+"F26.wireOp",EDGE,"E73.sketch_text.stroke-255")}),-1.0]])]});
            extrude(context, id + "F27", {"entities" : qUnion([Q0, Q1, Q2, Q3, Q4, Q5, Q6, Q7, Q8, Q9, Q10, Q11, Q12]), "operationType" : NewBodyOperationType.REMOVE, "oppositeDirection" : true, "depth" : .6 * mm});
        }
    });
